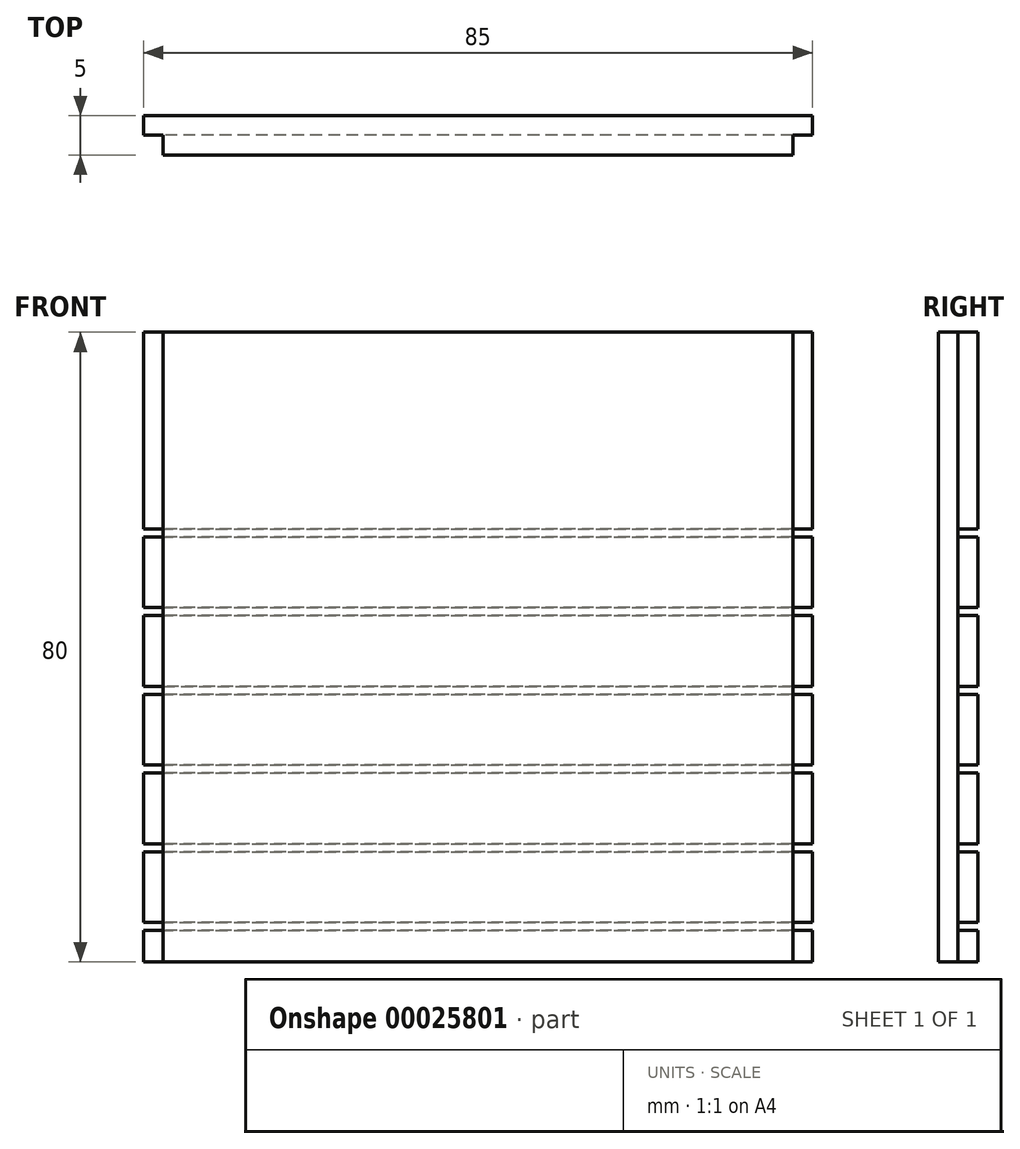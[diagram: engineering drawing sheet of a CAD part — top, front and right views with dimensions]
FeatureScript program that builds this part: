
annotation { "Feature Type Name" : "Feature", "Feature Type Description" : "" }
export const myFeature = defineFeature(function(context is Context, id is Id, definition is map)
    precondition{}
    {
        {
            var Q0;
            Q0=qCreatedBy(makeId("Top.planeOp"),FACE);
            var sketch = newSketch(context, id + "F0", { "sketchPlane" : qUnion([Q0])});
            skLineSegment(sketch, "E0.rect.bottom", {"start": v(-42.5, 2.5) * mm, "end": v(42.5, 2.5) * mm});
            skLineSegment(sketch, "E0.rect.top", {"start": v(-42.5, -2.5) * mm, "end": v(42.5, -2.5) * mm});
            skLineSegment(sketch, "E0.rect.left", {"start": v(-42.5, 2.5) * mm, "end": v(-42.5, -2.5) * mm});
            skLineSegment(sketch, "E0.rect.right", {"start": v(42.5, 2.5) * mm, "end": v(42.5, -2.5) * mm});
            skPoint(sketch, "E0.rect.middle", {"position": v(0, 0) * mm});
            skLineSegment(sketch, "E1.bottom", {"start": v(-42.5, -2.5) * mm, "end": v(-40, -2.5) * mm});
            skLineSegment(sketch, "E1.top", {"start": v(-42.5, 0) * mm, "end": v(-40, 0) * mm});
            skLineSegment(sketch, "E1.left", {"start": v(-42.5, -2.5) * mm, "end": v(-42.5, 0) * mm});
            skLineSegment(sketch, "E1.right", {"start": v(-40, -2.5) * mm, "end": v(-40, 0) * mm});
            skLineSegment(sketch, "E2.bottom", {"start": v(42.5, -2.5) * mm, "end": v(40, -2.5) * mm});
            skLineSegment(sketch, "E2.top", {"start": v(42.5, 0) * mm, "end": v(40, 0) * mm});
            skLineSegment(sketch, "E2.left", {"start": v(42.5, -2.5) * mm, "end": v(42.5, 0) * mm});
            skLineSegment(sketch, "E2.right", {"start": v(40, -2.5) * mm, "end": v(40, 0) * mm});
            skSolve(sketch);
        }
        {
            var Q0;
            Q0=makeQuery(id+"F0.imprint","IMPRINT",FACE,{"disambiguationData":[TD([[makeQuery(id+"F0.imprint","IMPRINT",EDGE,{"derivedFrom":sQuery(id+"F0.wireOp",EDGE,"E0.rect.bottom")}),-1.0]])]});
            extrude(context, id + "F1", {"entities" : qUnion([Q0]), "depth" : 40 * mm, "hasSecondDirection" : true, "secondDirectionOppositeDirection" : true, "secondDirectionDepth" : 40 * mm});
        }
        {
            var Q0;
            Q0=qCreatedBy(makeId("Front.planeOp"),FACE);
            var sketch = newSketch(context, id + "F2", { "sketchPlane" : qUnion([Q0])});
            skLineSegment(sketch, "E3.rect.bottom", {"start": v(42.5, -40) * mm, "end": v(-42.5, -40) * mm});
            skLineSegment(sketch, "E3.rect.top", {"start": v(42.5, 40) * mm, "end": v(-42.5, 40) * mm});
            skLineSegment(sketch, "E3.rect.left", {"start": v(42.5, -40) * mm, "end": v(42.5, 40) * mm});
            skLineSegment(sketch, "E3.rect.right", {"start": v(-42.5, -40) * mm, "end": v(-42.5, 40) * mm});
            skPoint(sketch, "E3.rect.middle", {"position": v(0, 0) * mm});
            skLineSegment(sketch, "E4.bottom", {"start": v(42.5, -36) * mm, "end": v(-42.5, -36) * mm});
            skLineSegment(sketch, "E4.top", {"start": v(42.5, -35) * mm, "end": v(-42.5, -35) * mm});
            skLineSegment(sketch, "E4.left", {"start": v(42.5, -36) * mm, "end": v(42.5, -35) * mm});
            skLineSegment(sketch, "E4.right", {"start": v(-42.5, -36) * mm, "end": v(-42.5, -35) * mm});
            skLineSegment(sketch, "E5.bottom", {"start": v(42.5, -26) * mm, "end": v(-42.5, -26) * mm});
            skLineSegment(sketch, "E5.top", {"start": v(42.5, -25) * mm, "end": v(-42.5, -25) * mm});
            skLineSegment(sketch, "E5.left", {"start": v(42.5, -26) * mm, "end": v(42.5, -25) * mm});
            skLineSegment(sketch, "E5.right", {"start": v(-42.5, -26) * mm, "end": v(-42.5, -25) * mm});
            skLineSegment(sketch, "E6.bottom", {"start": v(42.5, -16) * mm, "end": v(-42.5, -16) * mm});
            skLineSegment(sketch, "E6.top", {"start": v(42.5, 14) * mm, "end": v(-42.5, 14) * mm});
            skLineSegment(sketch, "E6.left", {"start": v(42.5, -16) * mm, "end": v(42.5, 14) * mm});
            skLineSegment(sketch, "E6.right", {"start": v(-42.5, -16) * mm, "end": v(-42.5, 14) * mm});
            skLineSegment(sketch, "E7.bottom", {"start": v(42.5, 15) * mm, "end": v(-42.5, 15) * mm});
            skLineSegment(sketch, "E8.bottom", {"start": v(42.5, -15) * mm, "end": v(-42.5, -15) * mm});
            skLineSegment(sketch, "E8.top", {"start": v(42.5, -6) * mm, "end": v(-42.5, -6) * mm});
            skLineSegment(sketch, "E8.left", {"start": v(42.5, -15) * mm, "end": v(42.5, -6) * mm});
            skLineSegment(sketch, "E8.right", {"start": v(-42.5, -15) * mm, "end": v(-42.5, -6) * mm});
            skLineSegment(sketch, "E9.bottom", {"start": v(-42.5, -6.16) * mm, "end": v(42.5, -6.16) * mm});
            skLineSegment(sketch, "E9.top", {"start": v(-42.5, -5) * mm, "end": v(42.5, -5) * mm});
            skLineSegment(sketch, "E9.left", {"start": v(-42.5, -6.16) * mm, "end": v(-42.5, -5) * mm});
            skLineSegment(sketch, "E9.right", {"start": v(42.5, -6.16) * mm, "end": v(42.5, -5) * mm});
            skLineSegment(sketch, "E10.bottom", {"start": v(42.5, 4) * mm, "end": v(-42.5, 4) * mm});
            skLineSegment(sketch, "E10.top", {"start": v(42.5, 5) * mm, "end": v(-42.5, 5) * mm});
            skLineSegment(sketch, "E10.left", {"start": v(42.5, 4) * mm, "end": v(42.5, 5) * mm});
            skLineSegment(sketch, "E10.right", {"start": v(-42.5, 4) * mm, "end": v(-42.5, 5) * mm});
            skSolve(sketch);
        }
        {
            var Q0;
            Q0=makeQuery(id+"F2.imprint","IMPRINT",FACE,{"disambiguationData":[TD([[makeQuery(id+"F2.imprint","IMPRINT",EDGE,{"derivedFrom":sQuery(id+"F2.wireOp",EDGE,"E4.bottom")}),-1.0]])]});
            var Q1;
            Q1=makeQuery(id+"F2.imprint","IMPRINT",FACE,{"disambiguationData":[TD([[makeQuery(id+"F2.imprint","IMPRINT",EDGE,{"derivedFrom":sQuery(id+"F2.wireOp",EDGE,"E5.bottom")}),-1.0]])]});
            var Q2;
            {var subQ2=sQuery(id+"F2.wireOp",EDGE,"E6.bottom");Q2=makeQuery(id+"F2.imprint","IMPRINT",FACE,{"disambiguationData":[TD([[makeQuery(id+"F2.imprint","IMPRINT",EDGE,{"derivedFrom":subQ2}),-1.0]])]});}
            var Q3;
            {var subQ2=sQuery(id+"F2.wireOp",EDGE,"E8.top");Q3=makeQuery(id+"F2.imprint","IMPRINT",FACE,{"disambiguationData":[TD([[makeQuery(id+"F2.imprint","IMPRINT",EDGE,{"derivedFrom":subQ2}),-1.0]])]});}
            var Q4;
            Q4=makeQuery(id+"F2.imprint","IMPRINT",FACE,{"disambiguationData":[TD([[makeQuery(id+"F2.imprint","IMPRINT",EDGE,{"derivedFrom":sQuery(id+"F2.wireOp",EDGE,"E10.bottom")}),-1.0]])]});
            var Q5;
            {var subQ1=sQuery(id+"F2.wireOp",EDGE,"E6.top");Q5=makeQuery(id+"F2.imprint","IMPRINT",FACE,{"disambiguationData":[TD([[makeQuery(id+"F2.imprint","IMPRINT",EDGE,{"derivedFrom":subQ1}),-1.0]])]});}
            extrude(context, id + "F3", {"entities" : qUnion([Q0, Q1, Q2, Q3, Q4, Q5]), "operationType" : NewBodyOperationType.REMOVE, "oppositeDirection" : true, "depth" : 25 * mm});
        }
    });
